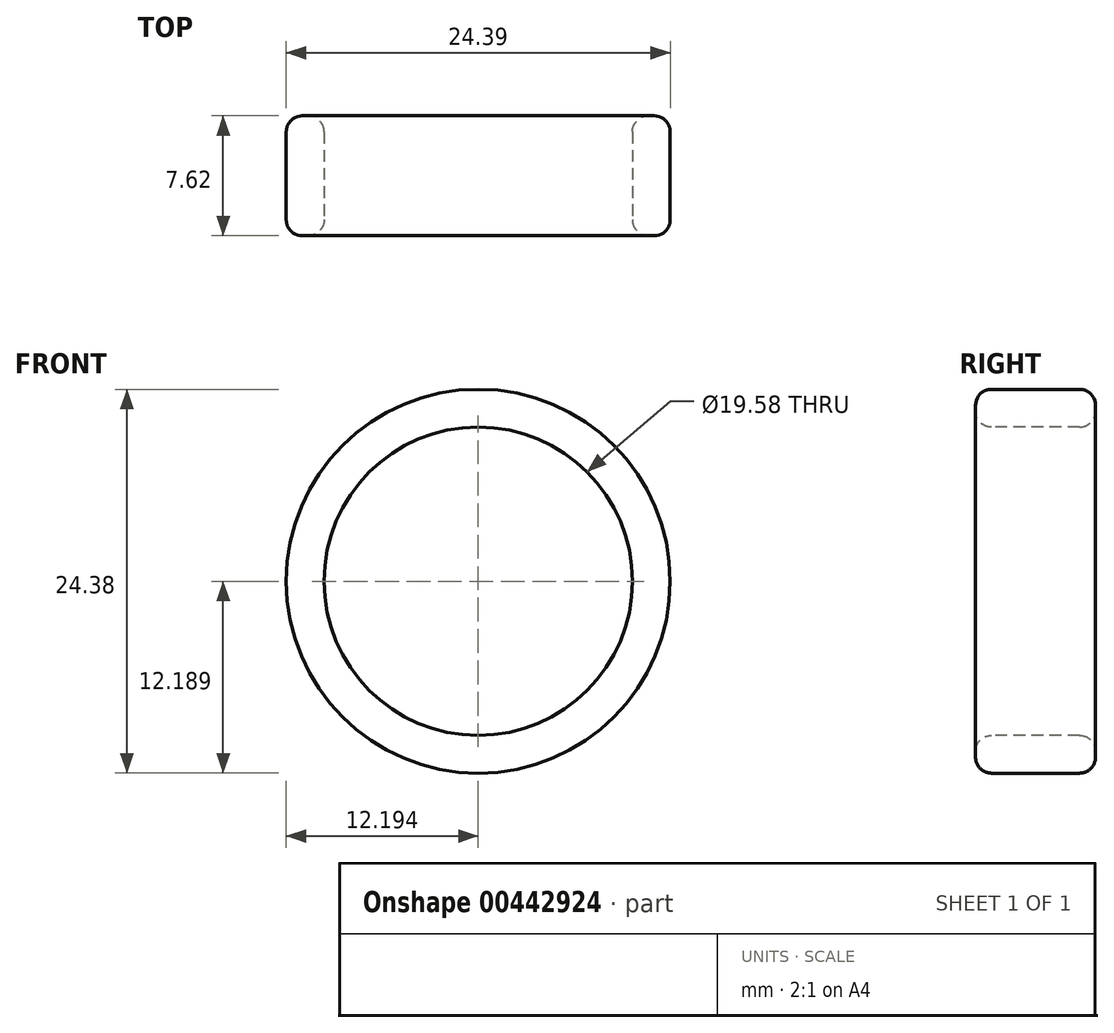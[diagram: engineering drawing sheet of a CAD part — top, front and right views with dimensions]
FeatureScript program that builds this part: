
annotation { "Feature Type Name" : "Feature", "Feature Type Description" : "" }
export const myFeature = defineFeature(function(context is Context, id is Id, definition is map)
    precondition{}
    {
        {
            var Q0;
            Q0=qCreatedBy(makeId("Front.planeOp"),FACE);
            var sketch = newSketch(context, id + "F0", { "sketchPlane" : qUnion([Q0])});
            skCircle(sketch, "E0", {"center": v(-31.95, 19.86) * mm, "radius": 12.2 * mm});
            skCircle(sketch, "E1", {"center": v(-31.95, 19.86) * mm, "radius": 9.79 * mm});
            skSolve(sketch);
        }
        {
            var Q0;
            Q0 = qSketchRegion(id + "F0", true);
            var Q1;
            Q1=makeQuery(id+"F0.imprint","IMPRINT",FACE,{"disambiguationData":[TD([[makeQuery(id+"F0.imprint","IMPRINT",EDGE,{"derivedFrom":sQuery(id+"F0.wireOp",EDGE,"E0")}),1.0]])]});
            extrude(context, id + "F1", {"entities" : qUnion([Q0, Q1]), "oppositeDirection" : true, "depth" : 5.08 * mm});
        }
        {
            var Q0;
            Q0 = qSketchRegion(id + "F0", true);
            extrude(context, id + "F2", {"entities" : qUnion([Q0]), "operationType" : NewBodyOperationType.ADD, "depth" : 2.54 * mm});
        }
        {
            var Q0;
            Q0=makeQuery(id+"F2.opExtrude","CAP_EDGE",EDGE,{"disambiguationData":[OSD([sQuery(id+"F0.wireOp",EDGE,"E0")])],"isStart":false});
            var Q1;
            Q1=makeQuery(id+"F2.opExtrude","CAP_EDGE",EDGE,{"disambiguationData":[OSD([sQuery(id+"F0.wireOp",EDGE,"E1")])],"isStart":false});
            var Q2;
            Q2=makeQuery(id+"F1.opExtrude","CAP_EDGE",EDGE,{"disambiguationData":[OSD([sQuery(id+"F0.wireOp",EDGE,"E1")])],"isStart":false});
            var Q3;
            Q3=makeQuery(id+"F1.opExtrude","CAP_EDGE",EDGE,{"disambiguationData":[OSD([sQuery(id+"F0.wireOp",EDGE,"E0")])],"isStart":false});
            fillet(context, id + "F3", {"entities" : qUnion([Q0, Q1, Q2, Q3]), "radius" : 1.02 * mm, "tangentPropagation" : true, "allowEdgeOverflow" : false});
        }
    });
